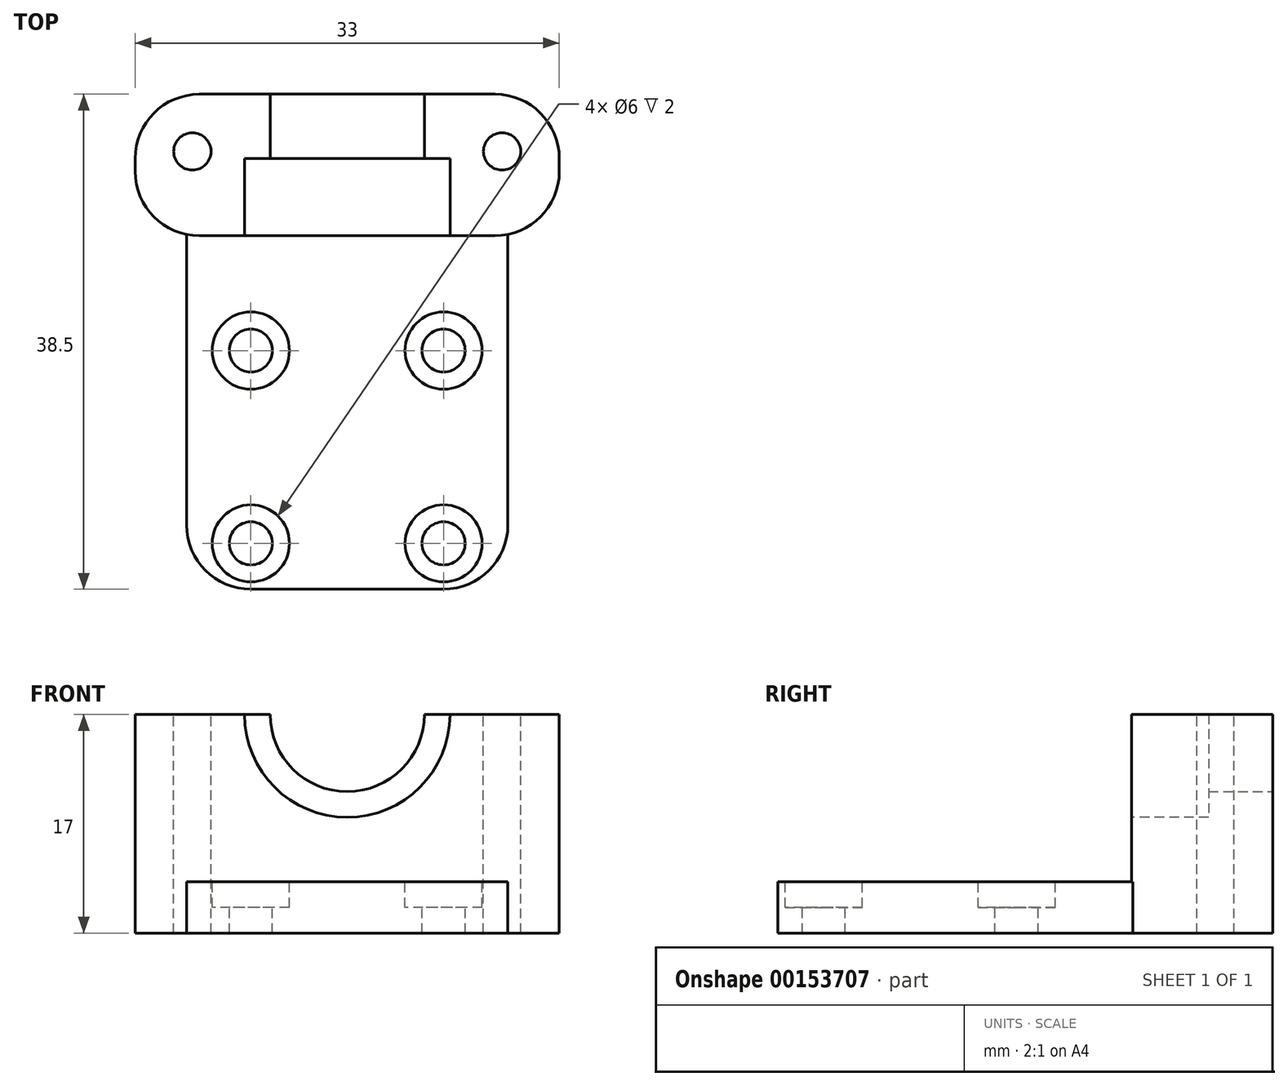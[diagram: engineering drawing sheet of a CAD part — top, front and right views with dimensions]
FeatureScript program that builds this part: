
annotation { "Feature Type Name" : "Feature", "Feature Type Description" : "" }
export const myFeature = defineFeature(function(context is Context, id is Id, definition is map)
    precondition{}
    {
        {
            var Q0;
            Q0=qCreatedBy(makeId("Top.planeOp"),FACE);
            var sketch = newSketch(context, id + "F0", { "sketchPlane" : qUnion([Q0])});
            skLineSegment(sketch, "E0.bottom", {"start": v(0, 0) * mm, "end": v(25, 0) * mm});
            skLineSegment(sketch, "E0.top", {"start": v(0, 38.5) * mm, "end": v(25, 38.5) * mm});
            skLineSegment(sketch, "E0.left", {"start": v(0, 0) * mm, "end": v(0, 38.5) * mm});
            skLineSegment(sketch, "E0.right", {"start": v(25, 0) * mm, "end": v(25, 38.5) * mm});
            skSolve(sketch);
        }
        {
            var Q0;
            Q0=qSketchRegion(id+"F0",true);
            extrude(context, id + "F1", {"entities" : qUnion([Q0]), "depth" : 4 * mm});
        }
        {
            var Q0;
            Q0=makeQuery(id+"F1.opExtrude","CAP_FACE",FACE,{"disambiguationData":[OSD([sQuery(id+"F0.wireOp",EDGE,"E0.bottom"),sQuery(id+"F0.wireOp",EDGE,"E0.top"),sQuery(id+"F0.wireOp",EDGE,"E0.left"),sQuery(id+"F0.wireOp",EDGE,"E0.right")])],"isStart":false});
            var sketch = newSketch(context, id + "F2", { "sketchPlane" : qUnion([Q0])});
            skCircle(sketch, "E1", {"center": v(5, 18.56) * mm, "radius": 1.68 * mm});
            skCircle(sketch, "E2", {"center": v(20, 18.56) * mm, "radius": 1.68 * mm});
            skCircle(sketch, "E3", {"center": v(5, 3.56) * mm, "radius": 1.68 * mm});
            skCircle(sketch, "E4", {"center": v(20, 3.56) * mm, "radius": 1.68 * mm});
            skLineSegment(sketch, "E5", {"start": v(5, 18.56) * mm, "end": v(0, 18.56) * mm});
            skLineSegment(sketch, "E6", {"start": v(20, 3.56) * mm, "end": v(25, 3.56) * mm});
            skCircle(sketch, "E7", {"center": v(5, 18.56) * mm, "radius": 3 * mm});
            skCircle(sketch, "E8", {"center": v(20, 18.56) * mm, "radius": 3 * mm});
            skCircle(sketch, "E9", {"center": v(5, 3.56) * mm, "radius": 3 * mm});
            skCircle(sketch, "E10", {"center": v(20, 3.56) * mm, "radius": 3 * mm});
            skSolve(sketch);
        }
        {
            var Q0;
            Q0=makeQuery(id+"F2.imprint","IMPRINT",FACE,{"disambiguationData":[TD([[makeQuery(id+"F2.imprint","IMPRINT",EDGE,{"derivedFrom":sQuery(id+"F2.wireOp",EDGE,"E1")}),1.0]])]});
            var Q1;
            Q1=makeQuery(id+"F2.imprint","IMPRINT",FACE,{"disambiguationData":[TD([[makeQuery(id+"F2.imprint","IMPRINT",EDGE,{"derivedFrom":sQuery(id+"F2.wireOp",EDGE,"E2")}),1.0]])]});
            var Q2;
            Q2=makeQuery(id+"F2.imprint","IMPRINT",FACE,{"disambiguationData":[TD([[makeQuery(id+"F2.imprint","IMPRINT",EDGE,{"derivedFrom":sQuery(id+"F2.wireOp",EDGE,"E4")}),1.0]])]});
            var Q3;
            Q3=makeQuery(id+"F2.imprint","IMPRINT",FACE,{"disambiguationData":[TD([[makeQuery(id+"F2.imprint","IMPRINT",EDGE,{"derivedFrom":sQuery(id+"F2.wireOp",EDGE,"E3")}),1.0]])]});
            extrude(context, id + "F3", {"entities" : qUnion([Q0, Q1, Q2, Q3]), "operationType" : NewBodyOperationType.REMOVE, "oppositeDirection" : true, "depth" : 25 * mm});
        }
        {
            var Q0;
            Q0=makeQuery(id+"F1.opExtrude","CAP_FACE",FACE,{"disambiguationData":[OSD([sQuery(id+"F0.wireOp",EDGE,"E0.bottom"),sQuery(id+"F0.wireOp",EDGE,"E0.top"),sQuery(id+"F0.wireOp",EDGE,"E0.left"),sQuery(id+"F0.wireOp",EDGE,"E0.right")])],"isStart":false});
            var sketch = newSketch(context, id + "F4", { "sketchPlane" : qUnion([Q0])});
            skLineSegment(sketch, "E11.bottom", {"start": v(0, 38.5) * mm, "end": v(25, 38.5) * mm});
            skLineSegment(sketch, "E11.top", {"start": v(0, 27.5) * mm, "end": v(25, 27.5) * mm});
            skLineSegment(sketch, "E11.left", {"start": v(0, 38.5) * mm, "end": v(0, 27.5) * mm});
            skLineSegment(sketch, "E11.right", {"start": v(25, 38.5) * mm, "end": v(25, 27.5) * mm});
            skSolve(sketch);
        }
        {
            var Q0;
            Q0=qSketchRegion(id+"F4",true);
            extrude(context, id + "F5", {"entities" : qUnion([Q0]), "operationType" : NewBodyOperationType.ADD, "depth" : 13 * mm});
        }
        {
            var Q0;
            Q0=makeQuery(id+"F5.boolean.opBoolean","MERGE",FACE,{"derivedFrom":[makeQuery(id+"F1.opExtrude","SWEPT_FACE",FACE,{"disambiguationData":[OSD([sQuery(id+"F0.wireOp",EDGE,"E0.top")])]}),makeQuery(id+"F5.opExtrude","SWEPT_FACE",FACE,{"disambiguationData":[OSD([sQuery(id+"F4.wireOp",EDGE,"E11.bottom")])]})]});
            var sketch = newSketch(context, id + "F6", { "sketchPlane" : qUnion([Q0])});
            skCircle(sketch, "E12", {"center": v(-12.5, 17) * mm, "radius": 6 * mm});
            skSolve(sketch);
        }
        {
            var Q0;
            {var subQ0=makeQuery(id+"F5.opExtrude","CAP_EDGE",EDGE,{"disambiguationData":[OSD([sQuery(id+"F4.wireOp",EDGE,"E11.bottom")])],"isStart":false});var subQ1=sQuery(id+"F6.wireOp",EDGE,"E12");var subQ3=makeQuery(id+"F6.imprint","INTERSECT",VERTEX,{"disambiguationData":[OD(0.0)],"derivedFrom":[subQ0,subQ1]});Q0=makeQuery(id+"F6.imprint","IMPRINT",FACE,{"disambiguationData":[TD([[makeQuery(id+"F6.imprint","IMPRINT",EDGE,{"disambiguationData":[TD([[subQ3,1.0]])],"derivedFrom":subQ1}),1.0]])]});}
            extrude(context, id + "F7", {"entities" : qUnion([Q0]), "operationType" : NewBodyOperationType.REMOVE, "oppositeDirection" : true, "depth" : 6 * mm});
        }
        {
            var Q0;
            Q0=makeQuery(id+"F5.opExtrude","SWEPT_FACE",FACE,{"disambiguationData":[OSD([sQuery(id+"F4.wireOp",EDGE,"E11.top")])]});
            var sketch = newSketch(context, id + "F8", { "sketchPlane" : qUnion([Q0])});
            skCircle(sketch, "E13", {"center": v(12.5, 17) * mm, "radius": 8 * mm});
            skSolve(sketch);
        }
        {
            var Q0;
            Q0=qSketchRegion(id+"F8",true);
            extrude(context, id + "F9", {"entities" : qUnion([Q0]), "operationType" : NewBodyOperationType.REMOVE, "oppositeDirection" : true, "depth" : 6 * mm});
        }
        {
            var Q0;
            Q0=makeQuery(id+"F2.imprint","IMPRINT",FACE,{"disambiguationData":[TD([[makeQuery(id+"F2.imprint","IMPRINT",EDGE,{"derivedFrom":sQuery(id+"F2.wireOp",EDGE,"E1")}),-1.0]])]});
            var Q1;
            Q1=makeQuery(id+"F2.imprint","IMPRINT",FACE,{"disambiguationData":[TD([[makeQuery(id+"F2.imprint","IMPRINT",EDGE,{"derivedFrom":sQuery(id+"F2.wireOp",EDGE,"E2")}),-1.0]])]});
            var Q2;
            Q2=makeQuery(id+"F2.imprint","IMPRINT",FACE,{"disambiguationData":[TD([[makeQuery(id+"F2.imprint","IMPRINT",EDGE,{"derivedFrom":sQuery(id+"F2.wireOp",EDGE,"E4")}),-1.0]])]});
            var Q3;
            Q3=makeQuery(id+"F2.imprint","IMPRINT",FACE,{"disambiguationData":[TD([[makeQuery(id+"F2.imprint","IMPRINT",EDGE,{"derivedFrom":sQuery(id+"F2.wireOp",EDGE,"E3")}),-1.0]])]});
            extrude(context, id + "F10", {"entities" : qUnion([Q0, Q1, Q2, Q3]), "operationType" : NewBodyOperationType.REMOVE, "oppositeDirection" : true, "depth" : 2 * mm});
        }
        {
            var Q0;
            Q0=makeQuery(id+"F5.boolean.opBoolean","MERGE",FACE,{"derivedFrom":[makeQuery(id+"F1.opExtrude","SWEPT_FACE",FACE,{"disambiguationData":[OSD([sQuery(id+"F0.wireOp",EDGE,"E0.left")])]}),makeQuery(id+"F5.opExtrude","SWEPT_FACE",FACE,{"disambiguationData":[OSD([sQuery(id+"F4.wireOp",EDGE,"E11.left")])]})]});
            var sketch = newSketch(context, id + "F11", { "sketchPlane" : qUnion([Q0])});
            skLineSegment(sketch, "E14.bottom", {"start": v(-38.5, 0) * mm, "end": v(-27.5, 0) * mm});
            skLineSegment(sketch, "E14.top", {"start": v(-38.5, 17) * mm, "end": v(-27.5, 17) * mm});
            skLineSegment(sketch, "E14.left", {"start": v(-38.5, 0) * mm, "end": v(-38.5, 17) * mm});
            skLineSegment(sketch, "E14.right", {"start": v(-27.5, 0) * mm, "end": v(-27.5, 17) * mm});
            skSolve(sketch);
        }
        {
            var Q0;
            Q0=qSketchRegion(id+"F11",true);
            extrude(context, id + "F12", {"entities" : qUnion([Q0]), "operationType" : NewBodyOperationType.ADD, "depth" : 4 * mm});
        }
        {
            var Q0;
            Q0=makeQuery(id+"F1.opExtrude","SWEPT_EDGE",EDGE,{"disambiguationData":[OSD([sQuery(id+"F0.wireOp",EDGE,"E0.bottom"),sQuery(id+"F0.wireOp",EDGE,"E0.left")])]});
            var Q1;
            Q1=makeQuery(id+"F1.opExtrude","SWEPT_EDGE",EDGE,{"disambiguationData":[OSD([sQuery(id+"F0.wireOp",EDGE,"E0.bottom"),sQuery(id+"F0.wireOp",EDGE,"E0.right")])]});
            fillet(context, id + "F13", {"entities" : qUnion([Q0, Q1]), "radius" : 5 * mm, "tangentPropagation" : true, "allowEdgeOverflow" : false});
        }
        {
            var Q0;
            Q0=makeQuery(id+"F5.boolean.opBoolean","MERGE",FACE,{"derivedFrom":[makeQuery(id+"F1.opExtrude","SWEPT_FACE",FACE,{"disambiguationData":[OSD([sQuery(id+"F0.wireOp",EDGE,"E0.right")])]}),makeQuery(id+"F5.opExtrude","SWEPT_FACE",FACE,{"disambiguationData":[OSD([sQuery(id+"F4.wireOp",EDGE,"E11.right")])]})]});
            var sketch = newSketch(context, id + "F14", { "sketchPlane" : qUnion([Q0])});
            skLineSegment(sketch, "E15.bottom", {"start": v(38.5, 0) * mm, "end": v(27.5, 0) * mm});
            skLineSegment(sketch, "E15.top", {"start": v(38.5, 17) * mm, "end": v(27.5, 17) * mm});
            skLineSegment(sketch, "E15.left", {"start": v(38.5, 0) * mm, "end": v(38.5, 17) * mm});
            skLineSegment(sketch, "E15.right", {"start": v(27.5, 0) * mm, "end": v(27.5, 17) * mm});
            skSolve(sketch);
        }
        {
            var Q0;
            Q0=qSketchRegion(id+"F14",true);
            extrude(context, id + "F15", {"entities" : qUnion([Q0]), "operationType" : NewBodyOperationType.ADD, "depth" : 4 * mm});
        }
        {
            var Q0;
            Q0=qSketchRegion(id+"F14",true);
            extrude(context, id + "F16", {"entities" : qUnion([Q0]), "operationType" : NewBodyOperationType.ADD, "depth" : 2 * mm});
        }
        {
            var Q0;
            {var subQ0=sQuery(id+"F4.wireOp",EDGE,"E11.bottom");var subQ1=sQuery(id+"F4.wireOp",EDGE,"E11.top");var subQ2=sQuery(id+"F4.wireOp",EDGE,"E11.left");Q0=makeQuery(id+"F9.boolean.opBoolean","SPLIT",FACE,{"disambiguationData":[TD([makeQuery(id+"F1.opExtrude","SWEPT_FACE",FACE,{"disambiguationData":[OSD([sQuery(id+"F0.wireOp",EDGE,"E0.left")])]})])],"derivedFrom":makeQuery(id+"F5.opExtrude","CAP_FACE",FACE,{"disambiguationData":[OSD([subQ0,subQ1,subQ2,sQuery(id+"F4.wireOp",EDGE,"E11.right")])],"isStart":false})});}
            var sketch = newSketch(context, id + "F17", { "sketchPlane" : qUnion([Q0])});
            skCircle(sketch, "E16", {"center": v(0.45, 34.05) * mm, "radius": 1.45 * mm});
            skCircle(sketch, "E17", {"center": v(24.55, 34.05) * mm, "radius": 1.45 * mm});
            skSolve(sketch);
        }
        {
            var Q0;
            Q0=qSketchRegion(id+"F17",true);
            extrude(context, id + "F18", {"entities" : qUnion([Q0]), "operationType" : NewBodyOperationType.REMOVE, "oppositeDirection" : true, "depth" : 25 * mm});
        }
        {
            var Q0;
            Q0=makeQuery(id+"F12.opExtrude","CAP_EDGE",EDGE,{"disambiguationData":[OSD([sQuery(id+"F11.wireOp",EDGE,"E14.left")])],"isStart":false});
            var Q1;
            Q1=makeQuery(id+"F12.opExtrude","CAP_EDGE",EDGE,{"disambiguationData":[OSD([sQuery(id+"F11.wireOp",EDGE,"E14.right")])],"isStart":false});
            var Q2;
            Q2=makeQuery(id+"F15.opExtrude","CAP_EDGE",EDGE,{"disambiguationData":[OSD([sQuery(id+"F14.wireOp",EDGE,"E15.right")])],"isStart":false});
            var Q3;
            Q3=makeQuery(id+"F15.opExtrude","CAP_EDGE",EDGE,{"disambiguationData":[OSD([sQuery(id+"F14.wireOp",EDGE,"E15.left")])],"isStart":false});
            fillet(context, id + "F19", {"entities" : qUnion([Q0, Q1, Q2, Q3]), "radius" : 5 * mm, "tangentPropagation" : true, "allowEdgeOverflow" : false});
        }
        {
            var Q0;
            Q0=makeQuery(id+"F2.imprint","IMPRINT",FACE,{"disambiguationData":[TD([[makeQuery(id+"F2.imprint","IMPRINT",EDGE,{"derivedFrom":sQuery(id+"F2.wireOp",EDGE,"E1")}),-1.0]])]});
            var Q1;
            Q1=makeQuery(id+"F2.imprint","IMPRINT",FACE,{"disambiguationData":[TD([[makeQuery(id+"F2.imprint","IMPRINT",EDGE,{"derivedFrom":sQuery(id+"F2.wireOp",EDGE,"E2")}),-1.0]])]});
            var Q2;
            Q2=makeQuery(id+"F2.imprint","IMPRINT",FACE,{"disambiguationData":[TD([[makeQuery(id+"F2.imprint","IMPRINT",EDGE,{"derivedFrom":sQuery(id+"F2.wireOp",EDGE,"E1")}),1.0]])]});
            var Q3;
            Q3=makeQuery(id+"F2.imprint","IMPRINT",FACE,{"disambiguationData":[TD([[makeQuery(id+"F2.imprint","IMPRINT",EDGE,{"derivedFrom":sQuery(id+"F2.wireOp",EDGE,"E2")}),1.0]])]});
            extrude(context, id + "F20", {"entities" : qUnion([Q0, Q1, Q2, Q3]), "operationType" : NewBodyOperationType.REMOVE, "depth" : 25 * mm});
        }
    });
